# Revit family: Support-Teknion-HWBFYD_hiSpace_Double_Sided_Frame-R2020
name_source: partatom
category: Furniture
units: mm (PartAtom-declared; Revit-internal decimal feet)

## family parameters
Always vertical = Yes
Cut with Voids When Loaded = No
OmniClass Number = 23.40.20.00
OmniClass Title = General Furniture and Specialties
Room Calculation Point = No
Shared = Yes
Work Plane-Based = No

## types (3) — shared parameters
Assembly Code = E2020200
Manufacturer = Teknion
Manufacturer Fax = 416.661.4586
Part Number = HWBFYD
Product Documentation Link = https://www.teknion.com
Product Line = hiSpace Double-Sided Bench
Product Page URL = https://www.teknion.com
Series = Height-Adjustable Bench hiSpace
Sustainability Data = https://www.teknion.com
URL = www.teknion.com
Unit Weight URL = http://www.teknion.com
Warranty = http://www.teknion.com
zero-valued in all types: Default Elevation

## per-type parameters (varying)
| type | 2D - Node for 9E | Description | Display with Up/Down Memory | Electrical | Extended Electric - Extended (22.6"-48.7") | Fixed Height (29") | Model | None | Toggle Display with Memory |
| Fixed Height (29"), No Switch | No | hiSpace Double-Sided Frame - Fixed Height (29") Base Mechanism, None Switch | No | No | No | Yes | HWBFYD2F____N | Yes | No |
| Extended Electric - Extended (22.6" - 48.7"), Display with Up/Down Memory Switch | Yes | hiSpace Double-Sided Frame - Extended Electric - Extended (22.6" - 48.7") Base Mechanism
, Display with Up/Down Memory Switch | Yes | Yes | Yes | No | HWBFYD9E____D | No | No |
| Extended Electric - Extended (22.6" - 48.7"), Toggle Display with Memory Switch | Yes | hiSpace Double-Sided Frame - Extended Electric - Extended (22.6" - 48.7") Base Mechanism
, Toggle Display with Memory Switch | No | Yes | Yes | No | HWBFYD9E____A | No | Yes |

## geometry (parser evidence)
native form markers: Sweep x4
no freeform markers — native parametric forms only
